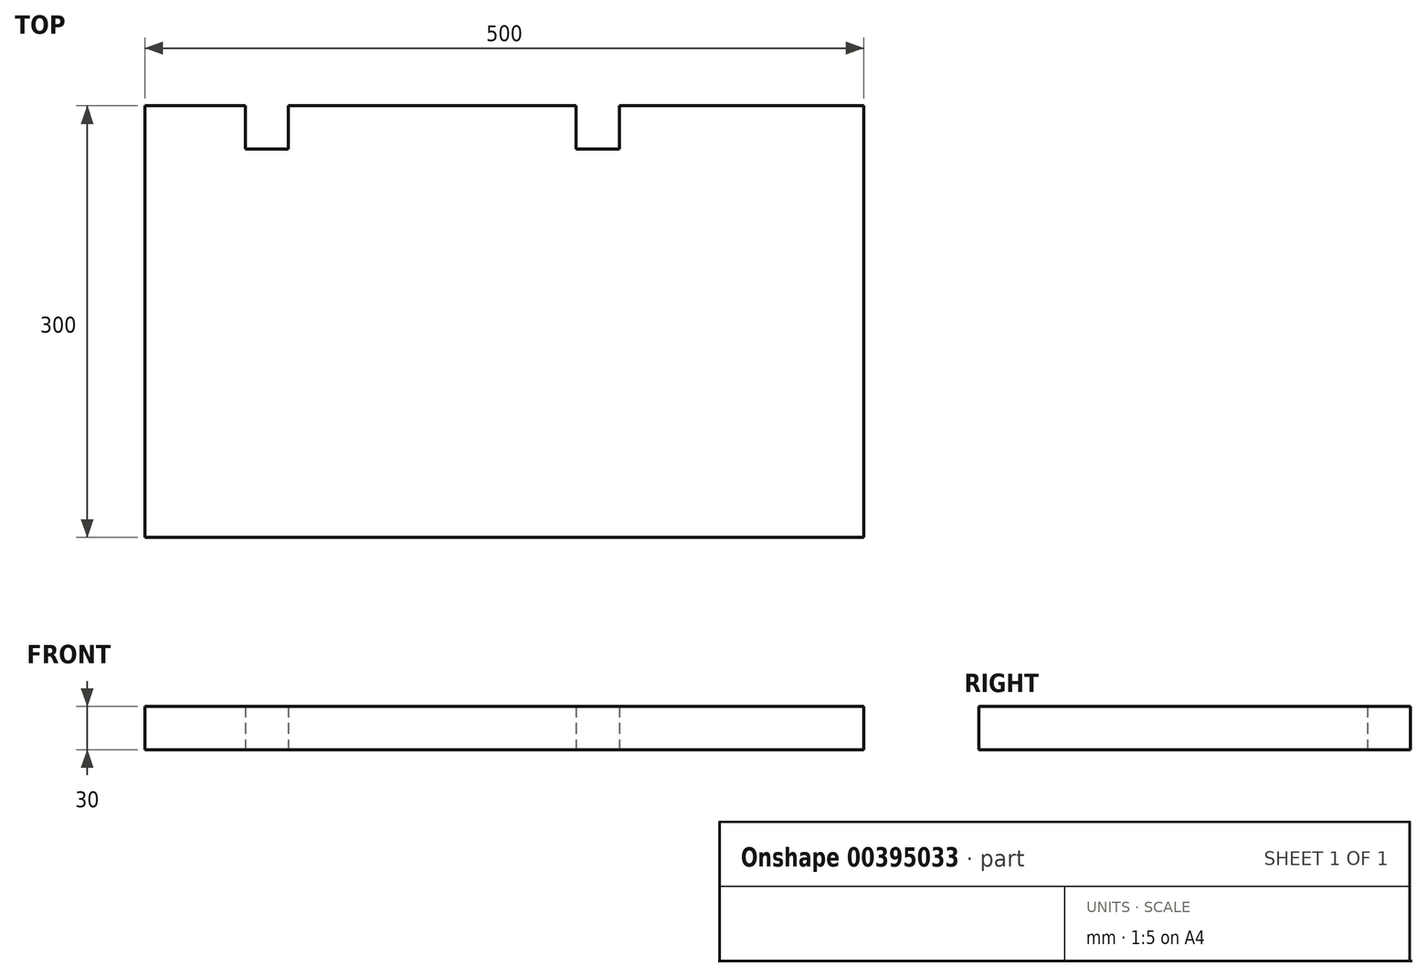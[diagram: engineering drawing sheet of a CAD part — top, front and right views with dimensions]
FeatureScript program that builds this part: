
annotation { "Feature Type Name" : "Feature", "Feature Type Description" : "" }
export const myFeature = defineFeature(function(context is Context, id is Id, definition is map)
    precondition{}
    {
        {
            var Q0;
            Q0=qCreatedBy(makeId("Front.planeOp"),FACE);
            var sketch = newSketch(context, id + "F0", { "sketchPlane" : qUnion([Q0])});
            skLineSegment(sketch, "E0.bottom", {"start": v(-250, 15) * mm, "end": v(250, 15) * mm});
            skLineSegment(sketch, "E0.top", {"start": v(-250, -15) * mm, "end": v(250, -15) * mm});
            skLineSegment(sketch, "E0.left", {"start": v(-250, 15) * mm, "end": v(-250, -15) * mm});
            skLineSegment(sketch, "E0.right", {"start": v(250, 15) * mm, "end": v(250, -15) * mm});
            skPoint(sketch, "E0.middle", {"position": v(0, 0) * mm});
            skSolve(sketch);
        }
        {
            var Q0;
            Q0=makeQuery(id+"F0.imprint","IMPRINT",FACE,{"disambiguationData":[TD([[makeQuery(id+"F0.imprint","IMPRINT",EDGE,{"derivedFrom":sQuery(id+"F0.wireOp",EDGE,"E0.bottom")}),-1.0]])]});
            extrude(context, id + "F1", {"entities" : qUnion([Q0]), "depth" : 300 * mm});
        }
        {
            var Q0;
            Q0=qCreatedBy(makeId("Front.planeOp"),FACE);
            var sketch = newSketch(context, id + "F2", { "sketchPlane" : qUnion([Q0])});
            skLineSegment(sketch, "E1.bottom", {"start": v(80, 15) * mm, "end": v(50, 15) * mm});
            skLineSegment(sketch, "E1.top", {"start": v(80, -15) * mm, "end": v(50, -15) * mm});
            skLineSegment(sketch, "E1.left", {"start": v(50, 15) * mm, "end": v(50, -15) * mm});
            skLineSegment(sketch, "E1.right", {"start": v(80, 15) * mm, "end": v(80, -15) * mm});
            skSolve(sketch);
        }
        {
            var Q0;
            Q0 = qSketchRegion(id + "F2", true);
            extrude(context, id + "F3", {"entities" : qUnion([Q0]), "operationType" : NewBodyOperationType.REMOVE, "depth" : 30 * mm});
        }
        {
            var Q0;
            Q0=qCreatedBy(makeId("Front.planeOp"),FACE);
            var sketch = newSketch(context, id + "F4", { "sketchPlane" : qUnion([Q0])});
            skLineSegment(sketch, "E2.bottom", {"start": v(-150, 15) * mm, "end": v(-180, 15) * mm});
            skLineSegment(sketch, "E2.top", {"start": v(-150, -15) * mm, "end": v(-180, -15) * mm});
            skLineSegment(sketch, "E2.left", {"start": v(-150, 15) * mm, "end": v(-150, -15) * mm});
            skLineSegment(sketch, "E2.right", {"start": v(-180, 15) * mm, "end": v(-180, -15) * mm});
            skSolve(sketch);
        }
        {
            var Q0;
            Q0 = qSketchRegion(id + "F4", true);
            extrude(context, id + "F5", {"entities" : qUnion([Q0]), "operationType" : NewBodyOperationType.REMOVE, "depth" : 30 * mm});
        }
    });
